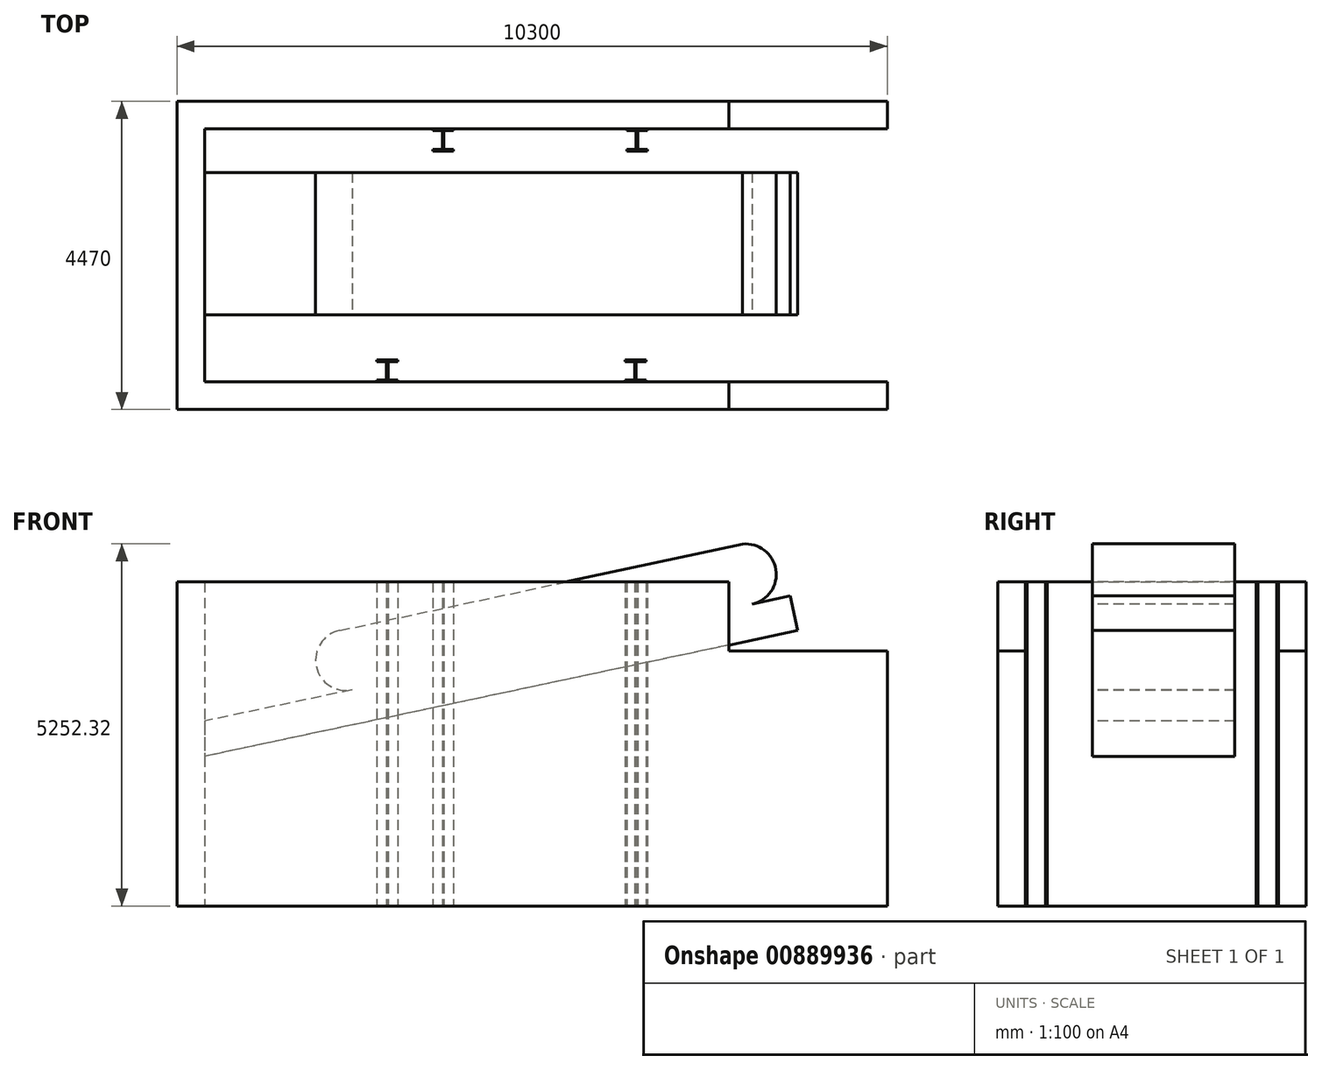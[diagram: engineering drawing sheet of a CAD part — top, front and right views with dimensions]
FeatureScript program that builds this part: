
annotation { "Feature Type Name" : "Feature", "Feature Type Description" : "" }
export const myFeature = defineFeature(function(context is Context, id is Id, definition is map)
    precondition{}
    {
        {
            var Q0;
            Q0=qCreatedBy(makeId("Top.planeOp"),FACE);
            var sketch = newSketch(context, id + "F0", { "sketchPlane" : qUnion([Q0])});
            skLineSegment(sketch, "E0", {"start": v(4950, 1835) * mm, "end": v(-4950, 1835) * mm});
            skLineSegment(sketch, "E1", {"start": v(-4950, 1835) * mm, "end": v(-4950, -1835) * mm});
            skLineSegment(sketch, "E2", {"start": v(-4950, -1835) * mm, "end": v(4950, -1835) * mm});
            skLineSegment(sketch, "E3", {"start": v(4950, -1835) * mm, "end": v(4950, -2235) * mm});
            skLineSegment(sketch, "E4", {"start": v(4950, -2235) * mm, "end": v(-5350, -2235) * mm});
            skLineSegment(sketch, "E5", {"start": v(-5350, -2235) * mm, "end": v(-5350, 2235) * mm});
            skLineSegment(sketch, "E6", {"start": v(-5350, 2235) * mm, "end": v(4950, 2235) * mm});
            skLineSegment(sketch, "E7", {"start": v(4950, 2235) * mm, "end": v(4950, 1835) * mm});
            skSolve(sketch);
        }
        {
            var Q0;
            Q0=qSketchRegion(id+"F0",true);
            extrude(context, id + "F1", {"entities" : qUnion([Q0]), "depth" : 4700 * mm, "offsetDistance" : 25 * mm});
        }
        {
            var Q0;
            Q0=makeQuery(id+"F1.opExtrude","SWEPT_FACE",FACE,{"disambiguationData":[OSD([sQuery(id+"F0.wireOp",EDGE,"E4")])]});
            var sketch = newSketch(context, id + "F2", { "sketchPlane" : qUnion([Q0])});
            skLineSegment(sketch, "E8", {"start": v(2650, 4700) * mm, "end": v(2650, 3700) * mm});
            skLineSegment(sketch, "E9", {"start": v(2650, 3700) * mm, "end": v(4950, 3700) * mm});
            skLineSegment(sketch, "E10", {"start": v(4950, 3700) * mm, "end": v(4950, 4700) * mm});
            skLineSegment(sketch, "E11", {"start": v(4950, 4700) * mm, "end": v(2650, 4700) * mm});
            skSolve(sketch);
        }
        {
            var Q0;
            Q0=qSketchRegion(id+"F2",true);
            extrude(context, id + "F3", {"entities" : qUnion([Q0]), "operationType" : NewBodyOperationType.REMOVE, "endBound" : BoundingType.THROUGH_ALL, "oppositeDirection" : true, "depth" : 25 * mm, "offsetDistance" : 25 * mm});
        }
        {
            var Q0;
            Q0=makeQuery(id+"F1.opExtrude","SWEPT_FACE",FACE,{"disambiguationData":[OSD([sQuery(id+"F0.wireOp",EDGE,"E2")])]});
            cPlane(context, id + "F4", {"entities" : qUnion([Q0]), "cplaneType" : CPlaneType.OFFSET, "offset" : 975 * mm, "width" : 150 * mm, "height" : 150 * mm});
        }
        {
            var Q0;
            Q0=qCreatedBy(id+"F4.planeOp",FACE);
            var sketch = newSketch(context, id + "F5", { "sketchPlane" : qUnion([Q0])});
            skLineSegment(sketch, "E12", {"start": v(0, 0) * mm, "end": v(4950, 0) * mm, "construction": true});
            skLineSegment(sketch, "E13", {"start": v(4950, 0) * mm, "end": v(4950, 2170) * mm, "construction": true});
            skLineSegment(sketch, "E14", {"start": v(2991.48, 3997.13) * mm, "end": v(-2850.14, 5249.6) * mm});
            skArc(sketch, "E15", {"start": v(2808.52, 3136.36) * mm, "mid": v(3329.62, 3475.42) * mm, "end": v(2991.48, 3997.13) * mm});
            skArc(sketch, "E16", {"start": v(-2850.14, 5249.6) * mm, "mid": v(-3334.4, 4881.97) * mm, "end": v(-2991.48, 4379.91) * mm});
            skLineSegment(sketch, "E17", {"start": v(2808.52, 3136.36) * mm, "end": v(4950, 2681.17) * mm});
            skLineSegment(sketch, "E18", {"start": v(4950, 2681.17) * mm, "end": v(4950, 2170) * mm});
            skLineSegment(sketch, "E19", {"start": v(-2991.48, 4379.91) * mm, "end": v(-3543.2, 4497.18) * mm});
            skLineSegment(sketch, "E20", {"start": v(-3543.2, 4497.18) * mm, "end": v(-3649.48, 3997.18) * mm});
            skLineSegment(sketch, "E21", {"start": v(-3649.48, 3997.18) * mm, "end": v(4950, 2170) * mm});
            skSolve(sketch);
        }
        {
            var Q0;
            Q0=qSketchRegion(id+"F5",true);
            extrude(context, id + "F6", {"entities" : qUnion([Q0]), "depth" : 2065 * mm, "offsetDistance" : 25 * mm});
        }
        {
            var Q0;
            Q0=qCreatedBy(makeId("Top.planeOp"),FACE);
            var sketch = newSketch(context, id + "F7", { "sketchPlane" : qUnion([Q0])});
            skLineSegment(sketch, "E22", {"start": v(-2450, -1835) * mm, "end": v(-2450, -1810) * mm});
            skLineSegment(sketch, "E23", {"start": v(-2450, -1810) * mm, "end": v(-2310, -1810) * mm});
            skLineSegment(sketch, "E24", {"start": v(-2290, -1540) * mm, "end": v(-2290, -1810) * mm});
            skLineSegment(sketch, "E25", {"start": v(-2290, -1810) * mm, "end": v(-2150, -1810) * mm});
            skLineSegment(sketch, "E26", {"start": v(-2150, -1810) * mm, "end": v(-2150, -1835) * mm});
            skLineSegment(sketch, "E27", {"start": v(-2150, -1835) * mm, "end": v(-2450, -1835) * mm});
            skLineSegment(sketch, "E28", {"start": v(-2310, -1810) * mm, "end": v(-2310, -1540) * mm});
            skLineSegment(sketch, "E29", {"start": v(-2310, -1540) * mm, "end": v(-2450, -1540) * mm});
            skLineSegment(sketch, "E30", {"start": v(-2450, -1540) * mm, "end": v(-2450, -1515) * mm});
            skLineSegment(sketch, "E31", {"start": v(-2150, -1515) * mm, "end": v(-2450, -1515) * mm});
            skLineSegment(sketch, "E32", {"start": v(-2290, -1540) * mm, "end": v(-2150, -1540) * mm});
            skLineSegment(sketch, "E33", {"start": v(-2150, -1540) * mm, "end": v(-2150, -1515) * mm});
            skLineSegment(sketch, "E34.MirrorCS", {"start": v(1150, -1540) * mm, "end": v(1150, -1515) * mm});
            skLineSegment(sketch, "E35.MirrorCS", {"start": v(1450, -1540) * mm, "end": v(1450, -1515) * mm});
            skLineSegment(sketch, "E36.MirrorCS", {"start": v(1150, -1810) * mm, "end": v(1150, -1835) * mm});
            skLineSegment(sketch, "E37.MirrorCS", {"start": v(1450, -1835) * mm, "end": v(1450, -1810) * mm});
            skLineSegment(sketch, "E38.MirrorCS", {"start": v(1290, -1540) * mm, "end": v(1150, -1540) * mm});
            skLineSegment(sketch, "E39.MirrorCS", {"start": v(1290, -1540) * mm, "end": v(1290, -1810) * mm});
            skLineSegment(sketch, "E40.MirrorCS", {"start": v(1310, -1540) * mm, "end": v(1450, -1540) * mm});
            skLineSegment(sketch, "E41.MirrorCS", {"start": v(1290, -1810) * mm, "end": v(1150, -1810) * mm});
            skLineSegment(sketch, "E42.MirrorCS", {"start": v(1450, -1810) * mm, "end": v(1310, -1810) * mm});
            skLineSegment(sketch, "E43.MirrorCS", {"start": v(1150, -1835) * mm, "end": v(1450, -1835) * mm});
            skLineSegment(sketch, "E44.MirrorCS", {"start": v(1150, -1515) * mm, "end": v(1450, -1515) * mm});
            skLineSegment(sketch, "E45.MirrorCS", {"start": v(1310, -1810) * mm, "end": v(1310, -1540) * mm});
            skLineSegment(sketch, "E46", {"start": v(0, 0) * mm, "end": v(-354.85, 0) * mm, "construction": true});
            skLineSegment(sketch, "E47", {"start": v(-1640, 1515) * mm, "end": v(-1640, 1540) * mm});
            skLineSegment(sketch, "E48", {"start": v(-1640, 1540) * mm, "end": v(-1500, 1540) * mm});
            skLineSegment(sketch, "E49", {"start": v(-1480, 1810) * mm, "end": v(-1480, 1540) * mm});
            skLineSegment(sketch, "E50", {"start": v(-1480, 1540) * mm, "end": v(-1340, 1540) * mm});
            skLineSegment(sketch, "E51", {"start": v(-1340, 1540) * mm, "end": v(-1340, 1515) * mm});
            skLineSegment(sketch, "E52", {"start": v(-1340, 1515) * mm, "end": v(-1640, 1515) * mm});
            skLineSegment(sketch, "E53", {"start": v(-1500, 1540) * mm, "end": v(-1500, 1810) * mm});
            skLineSegment(sketch, "E54", {"start": v(-1500, 1810) * mm, "end": v(-1640, 1810) * mm});
            skLineSegment(sketch, "E55", {"start": v(-1640, 1810) * mm, "end": v(-1640, 1835) * mm});
            skLineSegment(sketch, "E56", {"start": v(-1340, 1835) * mm, "end": v(-1640, 1835) * mm});
            skLineSegment(sketch, "E57", {"start": v(-1480, 1810) * mm, "end": v(-1340, 1810) * mm});
            skLineSegment(sketch, "E58", {"start": v(-1340, 1810) * mm, "end": v(-1340, 1835) * mm});
            skLineSegment(sketch, "E59", {"start": v(1170, 1515) * mm, "end": v(1170, 1540) * mm});
            skLineSegment(sketch, "E60", {"start": v(1170, 1540) * mm, "end": v(1310, 1540) * mm});
            skLineSegment(sketch, "E61", {"start": v(1330, 1810) * mm, "end": v(1330, 1540) * mm});
            skLineSegment(sketch, "E62", {"start": v(1330, 1540) * mm, "end": v(1470, 1540) * mm});
            skLineSegment(sketch, "E63", {"start": v(1470, 1540) * mm, "end": v(1470, 1515) * mm});
            skLineSegment(sketch, "E64", {"start": v(1470, 1515) * mm, "end": v(1170, 1515) * mm});
            skLineSegment(sketch, "E65", {"start": v(1310, 1540) * mm, "end": v(1310, 1810) * mm});
            skLineSegment(sketch, "E66", {"start": v(1310, 1810) * mm, "end": v(1170, 1810) * mm});
            skLineSegment(sketch, "E67", {"start": v(1170, 1810) * mm, "end": v(1170, 1835) * mm});
            skLineSegment(sketch, "E68", {"start": v(1470, 1835) * mm, "end": v(1170, 1835) * mm});
            skLineSegment(sketch, "E69", {"start": v(1330, 1810) * mm, "end": v(1470, 1810) * mm});
            skLineSegment(sketch, "E70", {"start": v(1470, 1810) * mm, "end": v(1470, 1835) * mm});
            skSolve(sketch);
        }
        {
            var Q0;
            Q0=qSketchRegion(id+"F7",true);
            extrude(context, id + "F8", {"entities" : qUnion([Q0]), "depth" : 4700 * mm, "offsetDistance" : 25 * mm});
        }
    });
